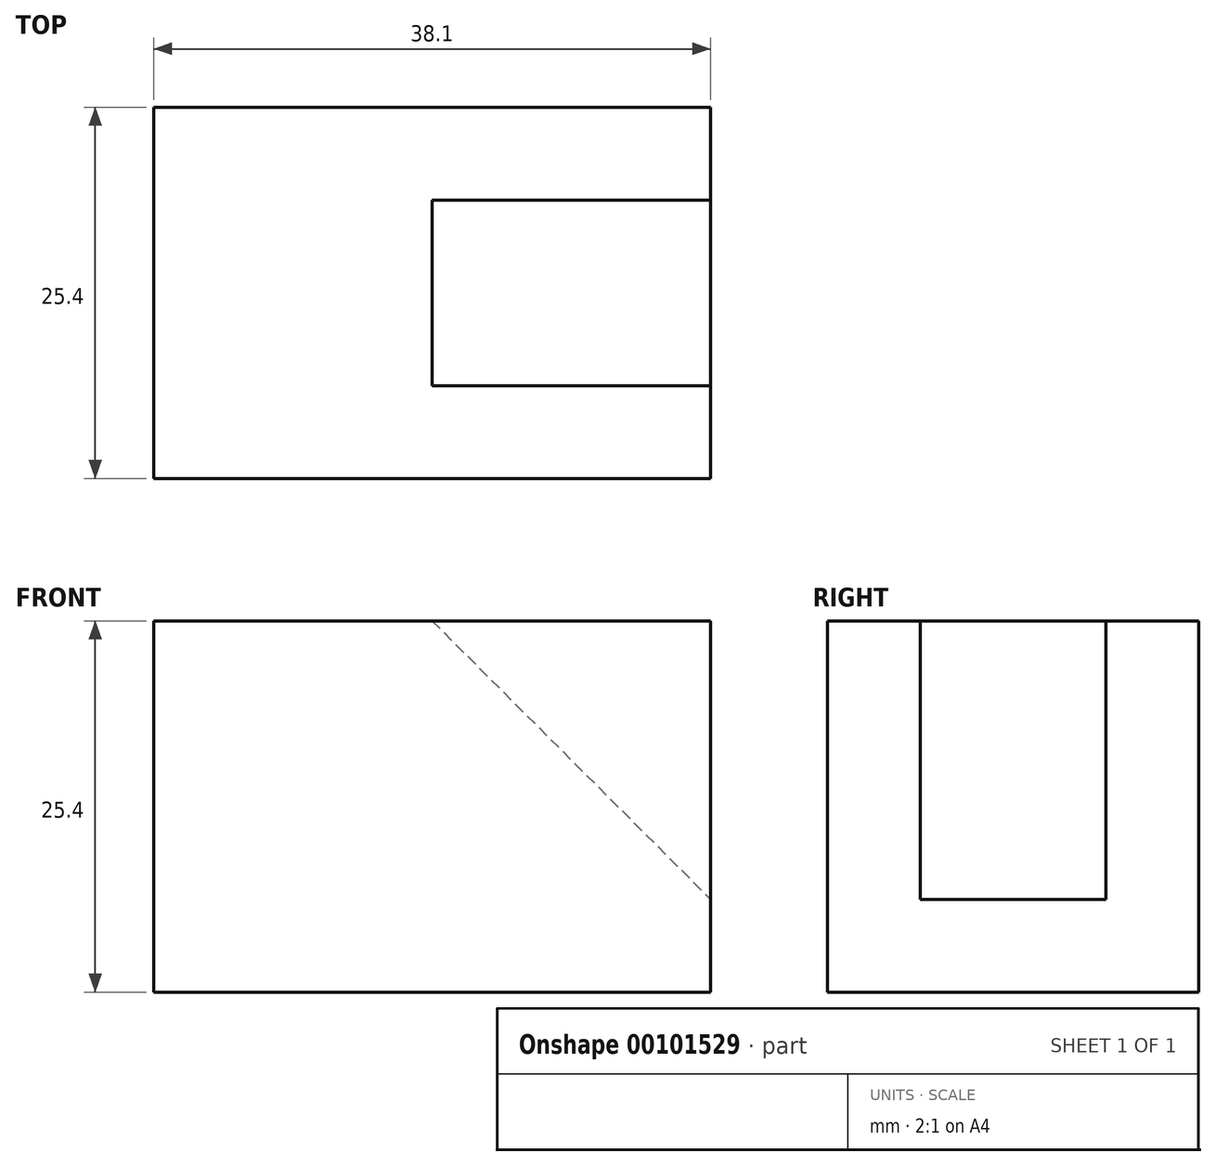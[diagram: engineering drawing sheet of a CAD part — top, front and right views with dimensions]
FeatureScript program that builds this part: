
annotation { "Feature Type Name" : "Feature", "Feature Type Description" : "" }
export const myFeature = defineFeature(function(context is Context, id is Id, definition is map)
    precondition{}
    {
        {
            var Q0;
            Q0=qCreatedBy(makeId("Front.planeOp"),FACE);
            var sketch = newSketch(context, id + "F0", { "sketchPlane" : qUnion([Q0])});
            skLineSegment(sketch, "E0", {"start": v(0, 0) * mm, "end": v(0, 25.4) * mm});
            skLineSegment(sketch, "E1", {"start": v(0, 25.4) * mm, "end": v(38.1, 25.4) * mm});
            skLineSegment(sketch, "E2", {"start": v(38.1, 25.4) * mm, "end": v(38.1, 0) * mm});
            skLineSegment(sketch, "E3", {"start": v(38.1, 0) * mm, "end": v(0, 0) * mm});
            skSolve(sketch);
        }
        {
            var Q0;
            Q0 = qSketchRegion(id + "F0", true);
            extrude(context, id + "F1", {"entities" : qUnion([Q0]), "depth" : 25.4 * mm});
        }
        {
            var Q0;
            Q0=makeQuery(id+"F1.opExtrude","CAP_FACE",FACE,{"disambiguationData":[OSD([sQuery(id+"F0.wireOp",EDGE,"E0"),sQuery(id+"F0.wireOp",EDGE,"E1"),sQuery(id+"F0.wireOp",EDGE,"E2"),sQuery(id+"F0.wireOp",EDGE,"E3")])],"isStart":false});
            var sketch = newSketch(context, id + "F2", { "sketchPlane" : qUnion([Q0])});
            skLineSegment(sketch, "E4", {"start": v(19.05, 25.4) * mm, "end": v(38.1, 25.4) * mm});
            skLineSegment(sketch, "E5", {"start": v(19.05, 25.4) * mm, "end": v(38.1, 6.35) * mm});
            skLineSegment(sketch, "E6", {"start": v(38.1, 25.4) * mm, "end": v(38.1, 6.35) * mm});
            skSolve(sketch);
        }
        {
            var Q0;
            Q0 = qSketchRegion(id + "F2", true);
            extrude(context, id + "F3", {"entities" : qUnion([Q0]), "operationType" : NewBodyOperationType.REMOVE, "oppositeDirection" : true, "depth" : 19.05 * mm, "hasSecondDirection" : true, "secondDirectionOppositeDirection" : true, "secondDirectionDepth" : 6.35 * mm});
        }
    });
